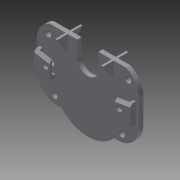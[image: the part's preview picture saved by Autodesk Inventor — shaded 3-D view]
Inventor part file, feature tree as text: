
AUTODESK INVENTOR PART (.ipt)
format: ipt  version: 2014 (Build 180170000, 170)  size: 261,632 bytes
history: native  units: mm
features: chamfer x7, extrude x6, sketch x6, projected_geometry x3, fillet x2
ambient origin geometry x8: Origin, YZ Plane, XZ Plane, XY Plane, X Axis, Y Axis, Z Axis, Center Point
bodies: Body1 (feature_tree)
feature tree (24):
  extrude  "押し出し8"  Depth=32.6mm
  fillet  "フィレット3"  Radius=48.6mm
  extrude  "押し出し9"  Depth=3.0mm
  extrude  "押し出し10"  Depth=3.0mm
  extrude  "押し出し11"  Depth=3.0mm
  extrude  "押し出し12"  Depth=3.0mm
  chamfer  "面取り3"  Distance=38.0mm
  chamfer  "面取り4"  Distance=32.0mm
  chamfer  "面取り5"  Distance=5.3mm
  extrude  "押し出し14"  Depth=8.3mm
  chamfer  "面取り6"  Distance=5.3mm
  chamfer  "面取り7"  [1 undecoded]
  chamfer  "面取り8"  Distance=3.6mm
  chamfer  "面取り9"  [1 undecoded]
  fillet  "フィレット5"  Radius=10.0mm
  sketch  "スケッチ8"
  sketch  "スケッチ9"
  sketch  "スケッチ10"
  sketch  "スケッチ11"
  projected_geometry  "投影ループ1"
  sketch  "スケッチ12"
  projected_geometry  "投影ループ2"
  sketch  "スケッチ14"
  projected_geometry  "投影ループ3"
note: 2 required parameter values undecoded (feature->parameter linkage not recoverable at this tier; creation-order binding heuristic only, values carry confidence <= 0.55)
